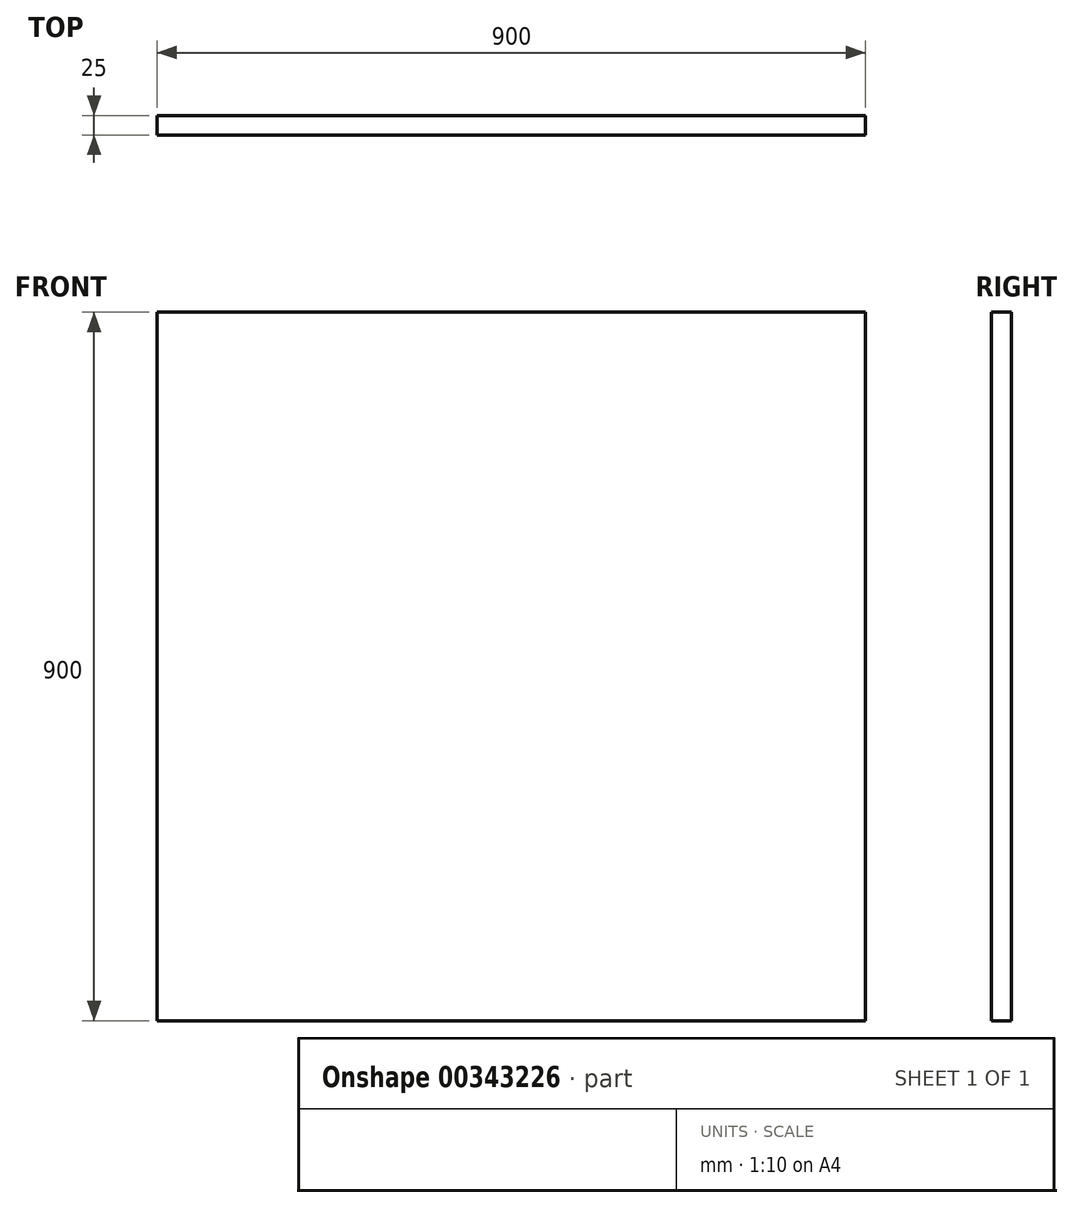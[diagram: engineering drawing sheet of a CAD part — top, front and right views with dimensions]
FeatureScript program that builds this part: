
annotation { "Feature Type Name" : "Feature", "Feature Type Description" : "" }
export const myFeature = defineFeature(function(context is Context, id is Id, definition is map)
    precondition{}
    {
        {
            var Q0;
            Q0=qCreatedBy(makeId("Front.planeOp"),FACE);
            var sketch = newSketch(context, id + "F0", { "sketchPlane" : qUnion([Q0])});
            skLineSegment(sketch, "E0.bottom", {"start": v(450, 450) * mm, "end": v(-450, 450) * mm});
            skLineSegment(sketch, "E0.top", {"start": v(450, -450) * mm, "end": v(-450, -450) * mm});
            skLineSegment(sketch, "E0.left", {"start": v(450, 450) * mm, "end": v(450, -450) * mm});
            skLineSegment(sketch, "E0.right", {"start": v(-450, 450) * mm, "end": v(-450, -450) * mm});
            skPoint(sketch, "E0.middle", {"position": v(0, 0) * mm});
            skSolve(sketch);
        }
        {
            var Q0;
            Q0=makeQuery(id+"F0.imprint","IMPRINT",FACE,{"disambiguationData":[TD([[makeQuery(id+"F0.imprint","IMPRINT",EDGE,{"derivedFrom":sQuery(id+"F0.wireOp",EDGE,"E0.bottom")}),1.0]])]});
            extrude(context, id + "F1", {"entities" : qUnion([Q0]), "depth" : 25 * mm});
        }
    });
